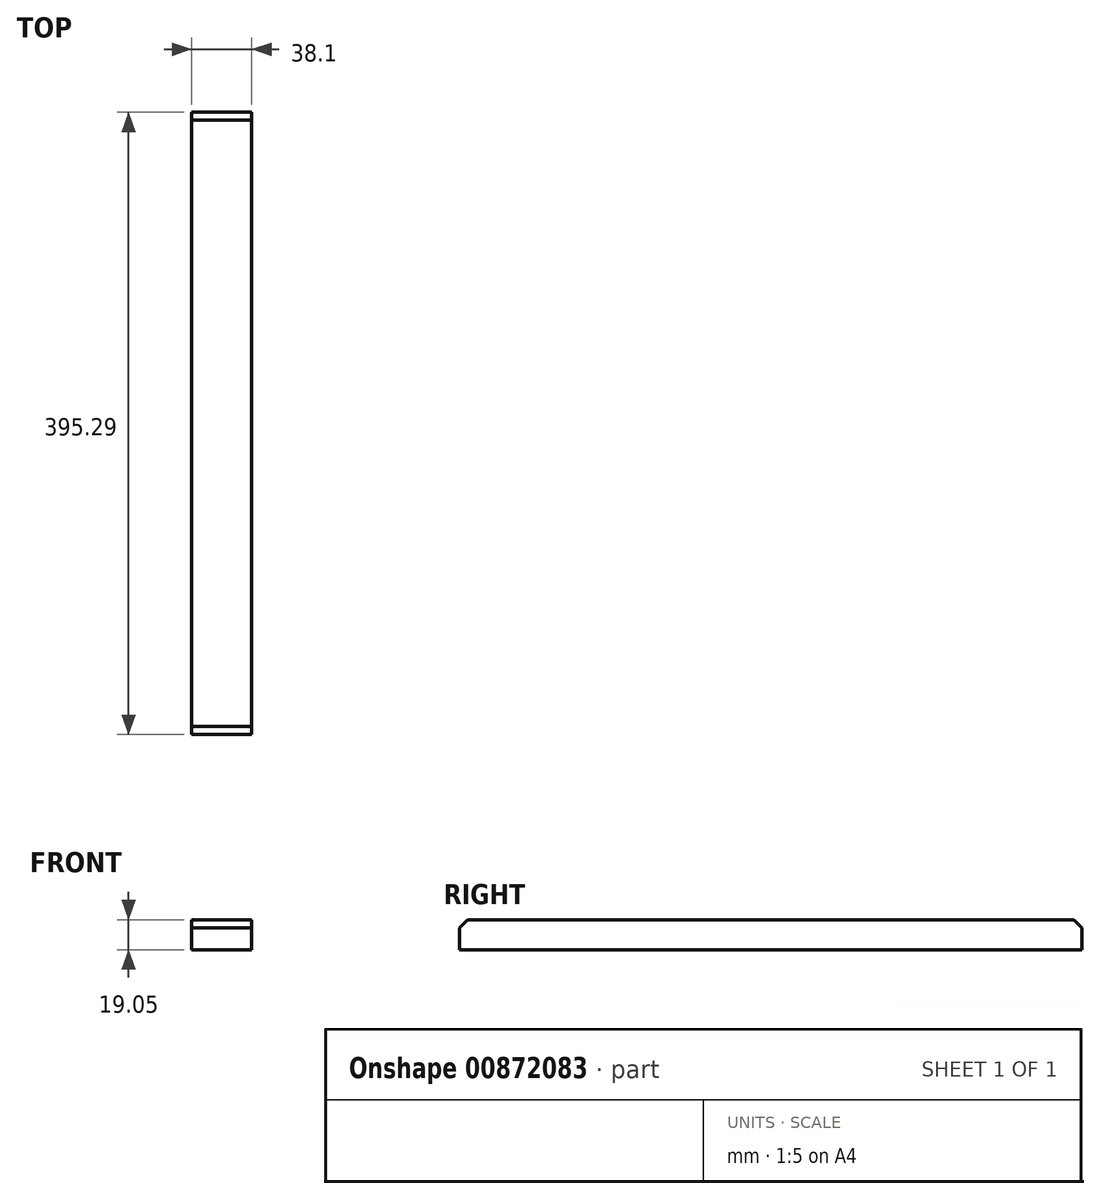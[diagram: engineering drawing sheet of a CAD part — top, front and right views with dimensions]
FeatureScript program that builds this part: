
annotation { "Feature Type Name" : "Feature", "Feature Type Description" : "" }
export const myFeature = defineFeature(function(context is Context, id is Id, definition is map)
    precondition{}
    {
        {
            var Q0;
            Q0=qCreatedBy(makeId("Front.planeOp"),FACE);
            var sketch = newSketch(context, id + "F0", { "sketchPlane" : qUnion([Q0])});
            skLineSegment(sketch, "E0.bottom", {"start": v(0, 0) * mm, "end": v(38.1, 0) * mm});
            skLineSegment(sketch, "E0.top", {"start": v(0, 19.05) * mm, "end": v(38.1, 19.05) * mm});
            skLineSegment(sketch, "E0.left", {"start": v(0, 0) * mm, "end": v(0, 19.05) * mm});
            skLineSegment(sketch, "E0.right", {"start": v(38.1, 0) * mm, "end": v(38.1, 19.05) * mm});
            skSolve(sketch);
        }
        {
            var Q0;
            Q0=qSketchRegion(id+"F0",true);
            extrude(context, id + "F1", {"entities" : qUnion([Q0]), "depth" : 395.3 * mm});
        }
        {
            var Q0;
            Q0=makeQuery(id+"F1.opExtrude","CAP_EDGE",EDGE,{"disambiguationData":[OSD([sQuery(id+"F0.wireOp",EDGE,"E0.top")])],"isStart":false});
            var Q1;
            Q1=makeQuery(id+"F1.opExtrude","CAP_EDGE",EDGE,{"disambiguationData":[OSD([sQuery(id+"F0.wireOp",EDGE,"E0.top")])],"isStart":true});
            chamfer(context, id + "F2", {"entities" : qUnion([Q0, Q1]), "width" : 5.08 * mm, "tangentPropagation" : true});
        }
    });
